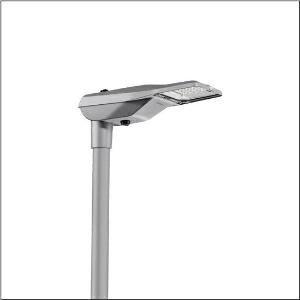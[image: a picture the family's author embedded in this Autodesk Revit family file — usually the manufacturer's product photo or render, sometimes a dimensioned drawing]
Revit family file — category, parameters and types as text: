
# Revit family: streetlight_sl_21_micro___st1_5a_5xe1p33t08db_27e3
name_source: partatom
category: Lighting Fixtures
units: mm (PartAtom-declared; Revit-internal decimal feet)

## family parameters
Cut with Voids When Loaded = No
Host = Face
Light Source = No
Part Type = Normal
Room Calculation Point = No
Round Connector Dimension = Use Diameter
Shared = No

## types (1)
- --- (1 x LED, 5020 lm, 39.1 W, 3000K)
    Apparent Load = 39 VA
    CIE Flux Codes = 22 53 95 100 100
    Color Rendering = 70
    Color Temperature = 3000K
    Default Elevation = 1800 mm
    Description = Streetlight SL 21 micro, mast luminaire, primary light control with lens, of PMMA, primary optical cover: cover, of toughened safety glass, transparent, light distribution: ST1.5a, light emission: direct distribution, primary light characteristic: asymmetric, installation type: side-entry, post-top, LED, High Power LED, rated luminous flux: 5.020lm, luminous efficacy: 128lm/W, light colour: 730, colour temperature: 3000K, control gear: D4i, control: flexible luminous flux parameterisation, time-dependent luminous flux control, constant luminous flux control, overheat protection, pre-setting: logarithmic dimming characteristic, mains connection: 220..240V, AC, 50/60Hz, start of lifetime: 39W, end of service life: 41W, reduction: 18W, luminaire housing, of diecast aluminium, powder-coated, Siteco® metallic grey (DB 702S), corrosivity category C5 mid according to DIN EN ISO 12944, please order mast flange separately, inclination adjustable: 0°, 5°, 10°, 15°, sealing non-destructively replaceable, multi-level sealing system, length: 528mm, width: 235mm, height: 110mm, mast flange for spigot size: 42mm (side-entry): 5XC10008XM4, 60/48mm (side-entry/post-top): 5XC10108XM2, 76/60mm (side-entry/post-top): 5XC10108XM1, Smart Interface below and above, protection rating (complete): IP66, insulation class (complete): insulation class II (safety insulation), certification: CE, ENEC, ENEC+, VDE, impact resistance: IK09, permissible operating ambient temperature for outdoor applications: -40..+50°C, standard-compliant lighting for roads and squares, packaging unit: 1 piece

Light Distribution: ST1.5a
    Height = 110 mm
    Lamp = 1 x LED
    Lamp Light Flux = 5020 lm
    Lamp Power = 39.1 W
    Lamp count = 1
    Length = 528 mm
    Luminous efficacy = 128 lm/W
    Manufacturer = Siteco
    ModVariant = No
    Model = 5XE1P33T08DB
    Number of Poles = 1
    OnlyDefault = Yes
    Power Factor = 1
    Product Name = Streetlight SL 21 micro | ST1.5a
    Product group = mast luminaire | pylon top
    ProductGroupID = 6100
    Protection Class = Protection class II
    Protection Degree = IP 66
    RLX_Detail_Level = 1
    RLX_Emergency_Light_Flux = 0 lm
    RLX_Emergency_Type = 0
    RLX_Emergency_Type_DB = No
    RlxData = <blob elided: 101717 chars, md5=f70ed39c>
    Socket = socket
    Standby Power = 0 W
    System Light Flux = 5020 lm
    System Power = 39 W
    Type Comments = factory setting: luminous flux: 100 % | dim-lin: 254 | 765 mA
    Type Image = l_1007239.jpg
    URL = http://relux.com
    VarID = @adj_149342
    Voltage = 0 V
    Weight = 0.00 kg
    Width = 235 mm

## geometry (parser evidence)
native form markers: Blend x4, Sweep x13
no freeform markers — native parametric forms only
